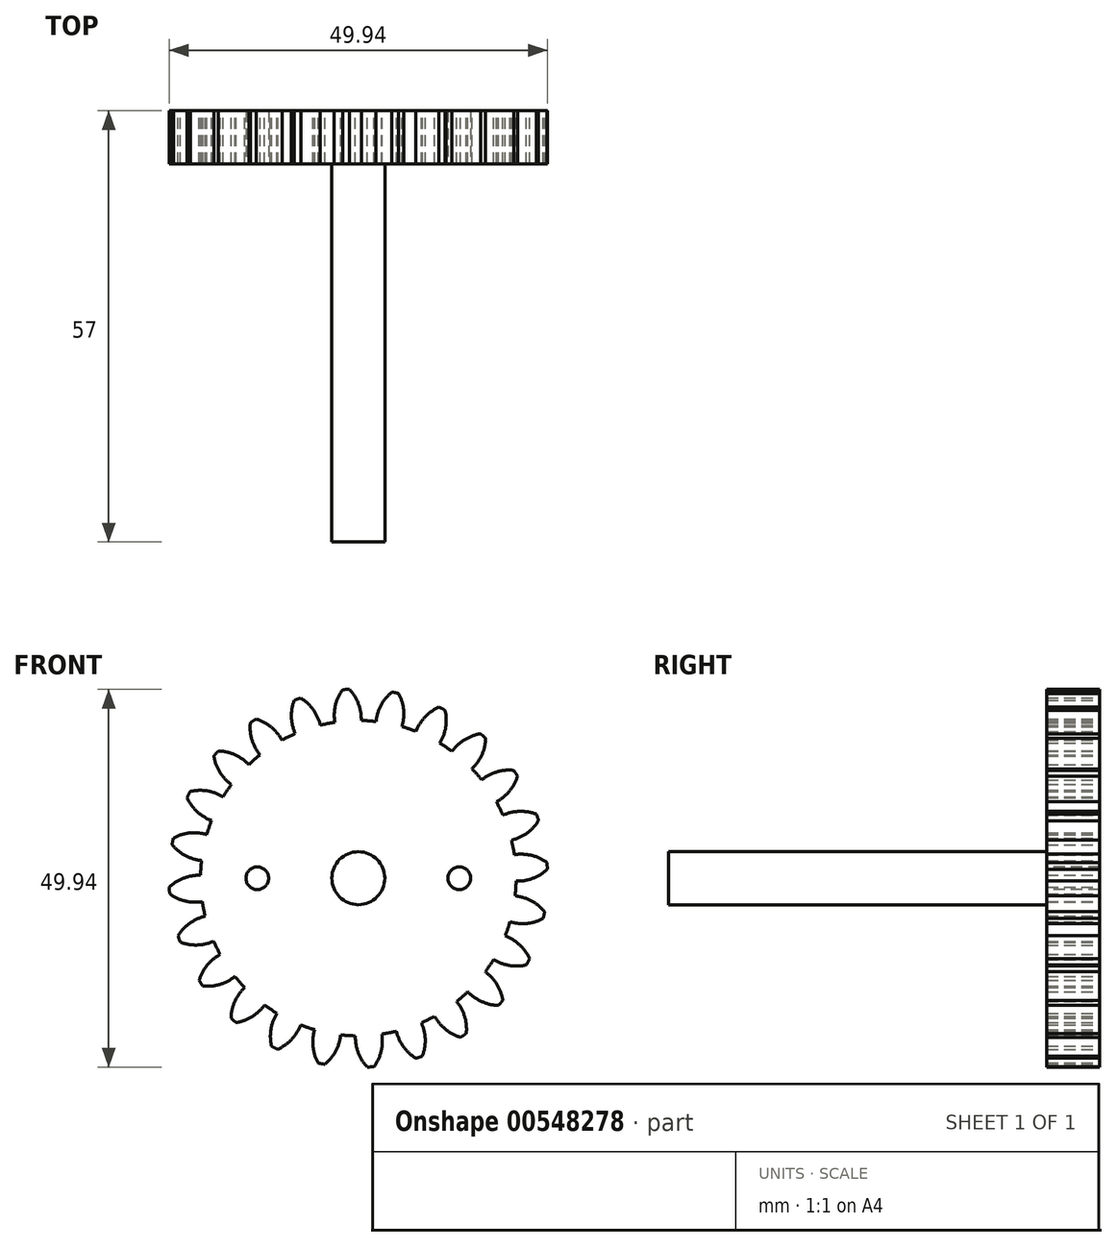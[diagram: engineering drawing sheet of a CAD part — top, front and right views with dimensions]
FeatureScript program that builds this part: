
annotation { "Feature Type Name" : "Feature", "Feature Type Description" : "" }
export const myFeature = defineFeature(function(context is Context, id is Id, definition is map)
    precondition{}
    {
        {
            var Q0;
            Q0=qCreatedBy(makeId("Front.planeOp"),FACE);
            var sketch = newSketch(context, id + "F0", { "sketchPlane" : qUnion([Q0])});
            skCircle(sketch, "E0", {"center": v(0, 0) * mm, "radius": 20.85 * mm});
            skCircle(sketch, "E1", {"center": v(0, 0) * mm, "radius": 23.1 * mm, "construction": true});
            skCircle(sketch, "E2", {"center": v(0, 0) * mm, "radius": 25 * mm, "construction": true});
            skLineSegment(sketch, "E3", {"start": v(0, 0) * mm, "end": v(0, 31.27) * mm, "construction": true});
            skLineSegment(sketch, "E4", {"start": v(0, 0) * mm, "end": v(-2.02, 30.85) * mm, "construction": true});
            skLineSegment(sketch, "E5", {"start": v(0, 23.1) * mm, "end": v(-25.24, 23.1) * mm, "construction": true});
            skLineSegment(sketch, "E6", {"start": v(0, 23.1) * mm, "end": v(-26.17, 13.58) * mm, "construction": true});
            skCircle(sketch, "E7", {"center": v(0, 23.1) * mm, "radius": 5.75 * mm, "construction": true});
            skCircle(sketch, "E8", {"center": v(0, 0) * mm, "radius": 21.7 * mm, "construction": true});
            skCircle(sketch, "E9", {"center": v(-5.36, 21.02) * mm, "radius": 5.75 * mm, "construction": true});
            skArc(sketch, "E10", {"start": v(0, 23.1) * mm, "mid": v(-0.5, 24.1) * mm, "end": v(-1.18, 24.97) * mm});
            skArc(sketch, "E11", {"start": v(0.39, 20.85) * mm, "mid": v(0.3, 22) * mm, "end": v(0, 23.1) * mm});
            skArc(sketch, "E12.MirrorCS", {"start": v(-3.1, 20.62) * mm, "mid": v(-3.17, 21.76) * mm, "end": v(-3.02, 22.9) * mm});
            skArc(sketch, "E13.MirrorCS", {"start": v(-3.02, 22.9) * mm, "mid": v(-2.65, 23.95) * mm, "end": v(-2.09, 24.91) * mm});
            skArc(sketch, "E14", {"start": v(-1.18, 24.97) * mm, "mid": v(-1.64, 24.96) * mm, "end": v(-2.09, 24.91) * mm});
            skSolve(sketch);
        }
        {
            var Q0;
            {var subQ0=sQuery(id+"F0.wireOp",EDGE,"E0");var subQ1=makeQuery(id+"F0.imprint","INTERSECT",VERTEX,{"derivedFrom":[subQ0,sQuery(id+"F0.wireOp",EDGE,"E11")]});Q0=makeQuery(id+"F0.imprint","IMPRINT",FACE,{"disambiguationData":[TD([[makeQuery(id+"F0.imprint","IMPRINT",EDGE,{"disambiguationData":[TD([[subQ1,-1.0]])],"derivedFrom":subQ0}),1.0]])]});}
            var Q1;
            Q1=makeQuery(id+"F0.imprint","IMPRINT",FACE,{"disambiguationData":[TD([[makeQuery(id+"F0.imprint","IMPRINT",EDGE,{"derivedFrom":sQuery(id+"F0.wireOp",EDGE,"E10")}),1.0]])]});
            extrude(context, id + "F1", {"entities" : qUnion([Q0, Q1]), "depth" : 7 * mm});
        }
        {
            var Q0;
            Q0=makeQuery(id+"F1.opExtrude","SWEPT_BODY",BODY,{"disambiguationData":[OSD([sQuery(id+"F0.wireOp",EDGE,"E0"),sQuery(id+"F0.wireOp",EDGE,"E10"),sQuery(id+"F0.wireOp",EDGE,"E11"),sQuery(id+"F0.wireOp",EDGE,"E12.MirrorCS"),sQuery(id+"F0.wireOp",EDGE,"E13.MirrorCS"),sQuery(id+"F0.wireOp",EDGE,"E14")])]});
            var Q1;
            Q1=makeQuery(id+"F1.opExtrude","SWEPT_FACE",FACE,{"disambiguationData":[OSD([sQuery(id+"F0.wireOp",EDGE,"E0")])]});
            circularPattern(context, id + "F2", {"operationType" : NewBodyOperationType.ADD, "entities" : qUnion([Q0]), "axis" : qUnion([Q1]), "angle" : 15 * degree, "instanceCount" : 24});
        }
        {
            var Q0;
            Q0=makeQuery(id+"F2.opPattern","COPY",FACE,{"derivedFrom":makeQuery(id+"F1.opExtrude","CAP_FACE",FACE,{"disambiguationData":[OSD([sQuery(id+"F0.wireOp",EDGE,"E0"),sQuery(id+"F0.wireOp",EDGE,"E10"),sQuery(id+"F0.wireOp",EDGE,"E11"),sQuery(id+"F0.wireOp",EDGE,"E12.MirrorCS"),sQuery(id+"F0.wireOp",EDGE,"E13.MirrorCS"),sQuery(id+"F0.wireOp",EDGE,"E14")])],"isStart":false}),"instanceName":"2"});
            var sketch = newSketch(context, id + "F3", { "sketchPlane" : qUnion([Q0])});
            skCircle(sketch, "E15", {"center": v(0, 0) * mm, "radius": 3.5 * mm});
            skCircle(sketch, "E16", {"center": v(-13.35, 0) * mm, "radius": 1.5 * mm});
            skCircle(sketch, "E17", {"center": v(13.35, 0) * mm, "radius": 1.5 * mm});
            skLineSegment(sketch, "E18", {"start": v(-11.85, 0) * mm, "end": v(11.85, 0) * mm, "construction": true});
            skSolve(sketch);
        }
        {
            var Q0;
            Q0=makeQuery(id+"F3.imprint","IMPRINT",FACE,{"disambiguationData":[TD([[makeQuery(id+"F3.imprint","IMPRINT",EDGE,{"derivedFrom":sQuery(id+"F3.wireOp",EDGE,"E15")}),1.0]])]});
            var Q1;
            Q1=sQuery(id+"F3.wireOp",EDGE,"E15");
            extrude(context, id + "F4", {"entities" : qUnion([Q0]), "operationType" : NewBodyOperationType.ADD, "surfaceEntities" : qUnion([Q1]), "depth" : 50 * mm});
        }
        {
            var Q0;
            Q0=makeQuery(id+"F3.imprint","IMPRINT",FACE,{"disambiguationData":[TD([[makeQuery(id+"F3.imprint","IMPRINT",EDGE,{"derivedFrom":sQuery(id+"F3.wireOp",EDGE,"E17")}),1.0]])]});
            var Q1;
            Q1=makeQuery(id+"F3.imprint","IMPRINT",FACE,{"disambiguationData":[TD([[makeQuery(id+"F3.imprint","IMPRINT",EDGE,{"derivedFrom":sQuery(id+"F3.wireOp",EDGE,"E16")}),1.0]])]});
            var Q2;
            {var subQ0=makeQuery(id+"F1.opExtrude","CAP_FACE",FACE,{"disambiguationData":[OSD([sQuery(id+"F0.wireOp",EDGE,"E0"),sQuery(id+"F0.wireOp",EDGE,"E10"),sQuery(id+"F0.wireOp",EDGE,"E11"),sQuery(id+"F0.wireOp",EDGE,"E12.MirrorCS"),sQuery(id+"F0.wireOp",EDGE,"E13.MirrorCS"),sQuery(id+"F0.wireOp",EDGE,"E14")])],"isStart":true});Q2=makeQuery(id+"F2.boolean.opBoolean","MERGE",FACE,{"derivedFrom":[subQ0,makeQuery(id+"F2.opPattern","COPY",FACE,{"derivedFrom":subQ0,"instanceName":"1"}),makeQuery(id+"F2.opPattern","COPY",FACE,{"derivedFrom":subQ0,"instanceName":"2"}),makeQuery(id+"F2.opPattern","COPY",FACE,{"derivedFrom":subQ0,"instanceName":"3"}),makeQuery(id+"F2.opPattern","COPY",FACE,{"derivedFrom":subQ0,"instanceName":"4"}),makeQuery(id+"F2.opPattern","COPY",FACE,{"derivedFrom":subQ0,"instanceName":"5"}),makeQuery(id+"F2.opPattern","COPY",FACE,{"derivedFrom":subQ0,"instanceName":"6"}),makeQuery(id+"F2.opPattern","COPY",FACE,{"derivedFrom":subQ0,"instanceName":"7"}),makeQuery(id+"F2.opPattern","COPY",FACE,{"derivedFrom":subQ0,"instanceName":"8"}),makeQuery(id+"F2.opPattern","COPY",FACE,{"derivedFrom":subQ0,"instanceName":"9"}),makeQuery(id+"F2.opPattern","COPY",FACE,{"derivedFrom":subQ0,"instanceName":"10"}),makeQuery(id+"F2.opPattern","COPY",FACE,{"derivedFrom":subQ0,"instanceName":"11"}),makeQuery(id+"F2.opPattern","COPY",FACE,{"derivedFrom":subQ0,"instanceName":"12"}),makeQuery(id+"F2.opPattern","COPY",FACE,{"derivedFrom":subQ0,"instanceName":"13"}),makeQuery(id+"F2.opPattern","COPY",FACE,{"derivedFrom":subQ0,"instanceName":"14"}),makeQuery(id+"F2.opPattern","COPY",FACE,{"derivedFrom":subQ0,"instanceName":"15"}),makeQuery(id+"F2.opPattern","COPY",FACE,{"derivedFrom":subQ0,"instanceName":"16"}),makeQuery(id+"F2.opPattern","COPY",FACE,{"derivedFrom":subQ0,"instanceName":"17"}),makeQuery(id+"F2.opPattern","COPY",FACE,{"derivedFrom":subQ0,"instanceName":"18"}),makeQuery(id+"F2.opPattern","COPY",FACE,{"derivedFrom":subQ0,"instanceName":"19"}),makeQuery(id+"F2.opPattern","COPY",FACE,{"derivedFrom":subQ0,"instanceName":"20"}),makeQuery(id+"F2.opPattern","COPY",FACE,{"derivedFrom":subQ0,"instanceName":"21"}),makeQuery(id+"F2.opPattern","COPY",FACE,{"derivedFrom":subQ0,"instanceName":"22"}),makeQuery(id+"F2.opPattern","COPY",FACE,{"derivedFrom":subQ0,"instanceName":"23"})]});}
            extrude(context, id + "F5", {"entities" : qUnion([Q0, Q1]), "operationType" : NewBodyOperationType.REMOVE, "endBound" : BoundingType.UP_TO_SURFACE, "oppositeDirection" : true, "endBoundEntityFace" : qUnion([Q2]), "depth" : 25 * mm});
        }
    });
